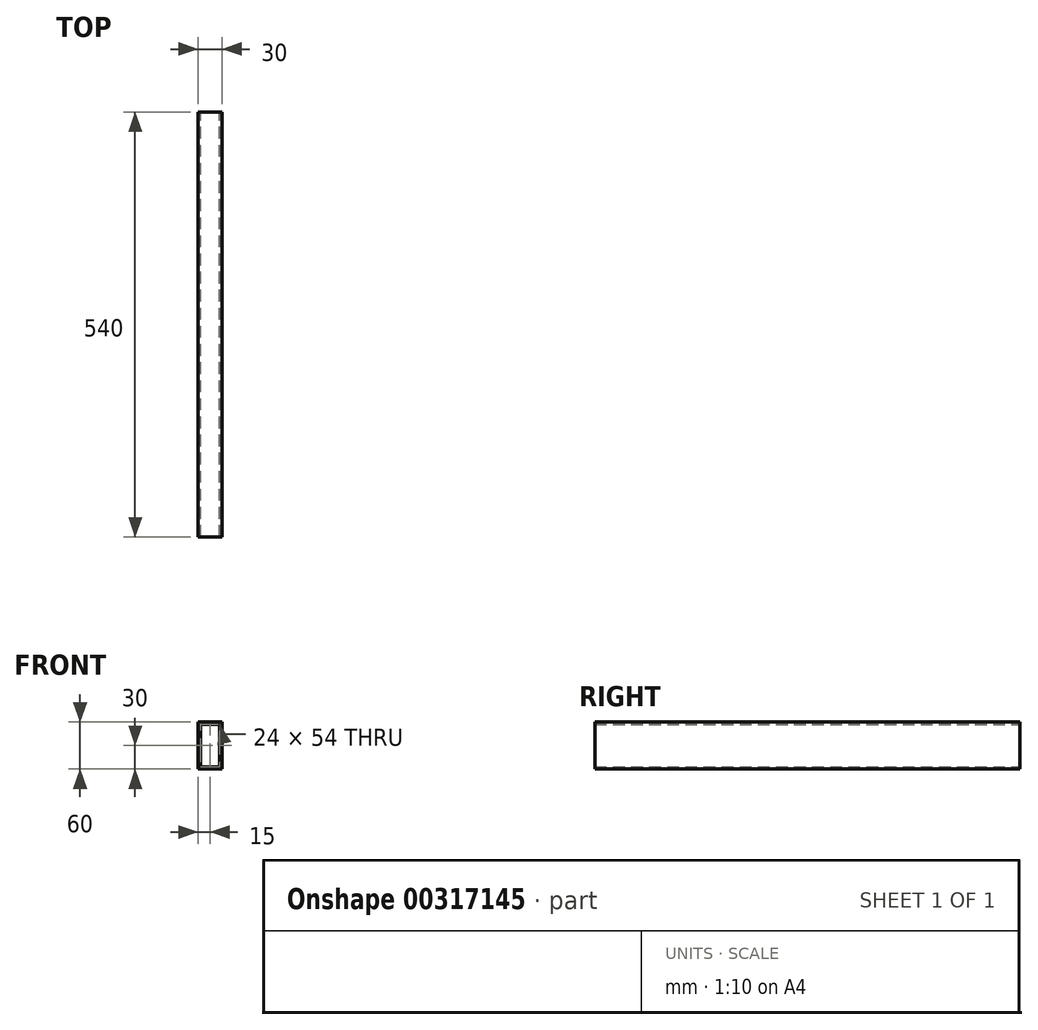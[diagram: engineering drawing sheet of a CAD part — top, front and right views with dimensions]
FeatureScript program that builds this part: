
annotation { "Feature Type Name" : "Feature", "Feature Type Description" : "" }
export const myFeature = defineFeature(function(context is Context, id is Id, definition is map)
    precondition{}
    {
        {
            var Q0;
            Q0=qCreatedBy(makeId("Front.planeOp"),FACE);
            var sketch = newSketch(context, id + "F0", { "sketchPlane" : qUnion([Q0])});
            skLineSegment(sketch, "E0.bottom", {"start": v(15, 30) * mm, "end": v(-15, 30) * mm});
            skLineSegment(sketch, "E0.top", {"start": v(15, -30) * mm, "end": v(-15, -30) * mm});
            skLineSegment(sketch, "E0.left", {"start": v(15, 30) * mm, "end": v(15, -30) * mm});
            skLineSegment(sketch, "E0.right", {"start": v(-15, 30) * mm, "end": v(-15, -30) * mm});
            skPoint(sketch, "E0.middle", {"position": v(0, 0) * mm});
            skLineSegment(sketch, "E1.0", {"start": v(12, -27) * mm, "end": v(-12, -27) * mm});
            skLineSegment(sketch, "E1.1", {"start": v(12, 27) * mm, "end": v(12, -27) * mm});
            skLineSegment(sketch, "E1.2", {"start": v(12, 27) * mm, "end": v(-12, 27) * mm});
            skLineSegment(sketch, "E1.3", {"start": v(-12, 27) * mm, "end": v(-12, -27) * mm});
            skSolve(sketch);
        }
        {
            var Q0;
            Q0=makeQuery(id+"F0.imprint","IMPRINT",FACE,{"disambiguationData":[TD([[makeQuery(id+"F0.imprint","IMPRINT",EDGE,{"derivedFrom":sQuery(id+"F0.wireOp",EDGE,"E0.bottom")}),1.0]])]});
            extrude(context, id + "F1", {"entities" : qUnion([Q0]), "endBound" : BoundingType.SYMMETRIC, "depth" : 540 * mm});
        }
    });
